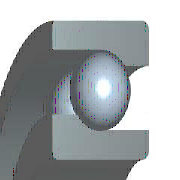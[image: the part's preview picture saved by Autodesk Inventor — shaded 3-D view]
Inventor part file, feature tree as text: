
AUTODESK INVENTOR PART (.ipt)
format: ipt  version: 2018 (Build 220112000, 112)  size: 311,296 bytes
history: native  units: mm (DEFAULTED — no unit token found)
features: other x5, plane x3, sketch x1, pattern_circular x1
ambient origin geometry x8: Origin, YZ Plane, XZ Plane, XY Plane, X Axis, Y Axis, Z Axis, Center Point
bodies: Solid1 (feature_tree)
feature tree (10):
  plane  "WorkPlane1"
  plane  "Work Plane2"
  plane  "WorkPlane2"
  other  "WorkPoint1"
  other  "WorkPoint3"
  other  "WorkPoint2"
  other  "WorkAxis1"
  sketch  "Schizzo7"
  other  "Work Axis2"
  pattern_circular  "Seriepolare1"  [2 undecoded]
note: 2 required parameter values undecoded (feature->parameter linkage not recoverable at this tier; creation-order binding heuristic only, values carry confidence <= 0.55)
